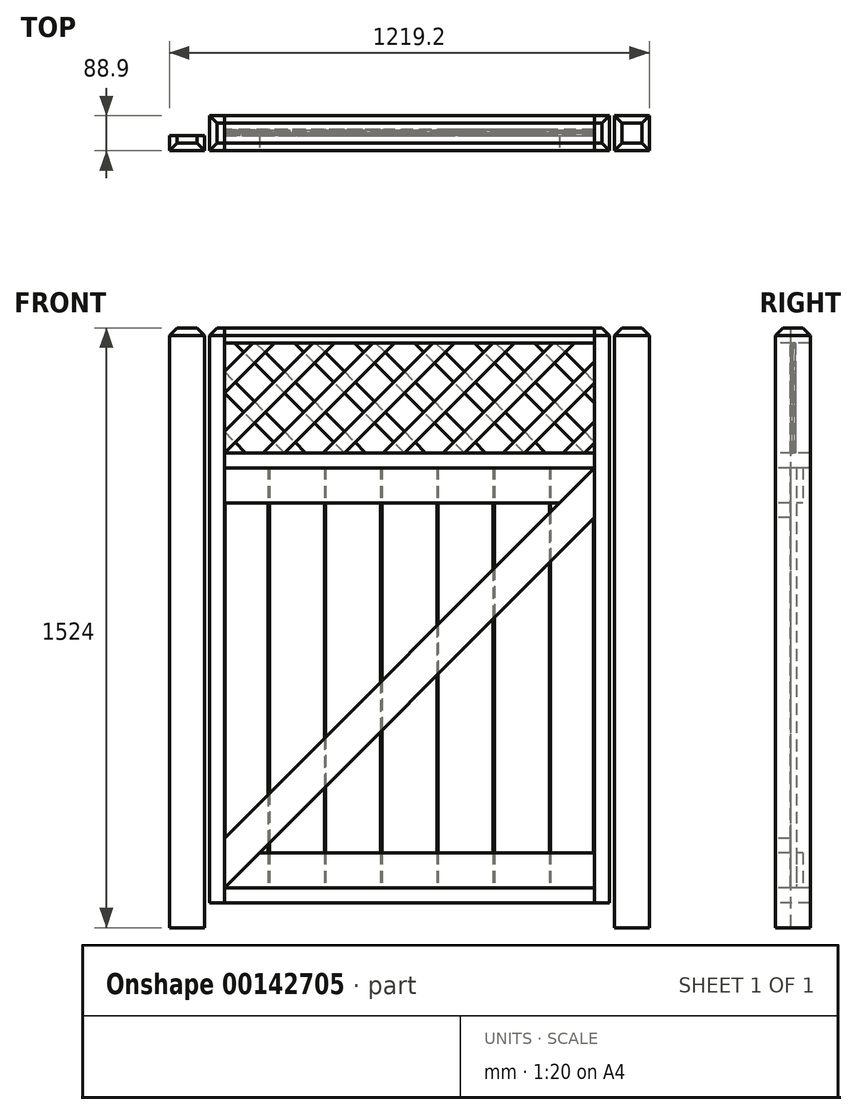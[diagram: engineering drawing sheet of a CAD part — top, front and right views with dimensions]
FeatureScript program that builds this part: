
annotation { "Feature Type Name" : "Feature", "Feature Type Description" : "" }
export const myFeature = defineFeature(function(context is Context, id is Id, definition is map)
    precondition{}
    {
        {
            var Q0;
            Q0=qCreatedBy(makeId("Top.planeOp"),FACE);
            var sketch = newSketch(context, id + "F0", { "sketchPlane" : qUnion([Q0])});
            skLineSegment(sketch, "E0", {"start": v(0, 0) * mm, "end": v(1250.95, 0) * mm, "construction": true});
            skLineSegment(sketch, "E1.bottom", {"start": v(1041.4, 0) * mm, "end": v(1130.3, 0) * mm});
            skLineSegment(sketch, "E1.top", {"start": v(1041.4, 88.9) * mm, "end": v(1130.3, 88.9) * mm});
            skLineSegment(sketch, "E1.left", {"start": v(1041.4, 0) * mm, "end": v(1041.4, 88.9) * mm});
            skLineSegment(sketch, "E1.right", {"start": v(1130.3, 0) * mm, "end": v(1130.3, 88.9) * mm});
            skLineSegment(sketch, "E2.bottom", {"start": v(0, 0) * mm, "end": v(-88.9, 0) * mm});
            skLineSegment(sketch, "E2.top", {"start": v(0, 38.1) * mm, "end": v(-88.9, 38.1) * mm});
            skLineSegment(sketch, "E2.left", {"start": v(0, 0) * mm, "end": v(0, 38.1) * mm});
            skLineSegment(sketch, "E2.right", {"start": v(-88.9, 0) * mm, "end": v(-88.9, 38.1) * mm});
            skSolve(sketch);
        }
        {
            var Q0;
            Q0 = qSketchRegion(id + "F0", true);
            extrude(context, id + "F1", {"entities" : qUnion([Q0]), "depth" : 1524 * mm});
        }
        {
            var Q0;
            Q0=makeQuery(id+"F1.opExtrude","SWEPT_FACE",FACE,{"disambiguationData":[OSD([sQuery(id+"F0.wireOp",EDGE,"E1.bottom")])]});
            var sketch = newSketch(context, id + "F2", { "sketchPlane" : qUnion([Q0])});
            skLineSegment(sketch, "E3.bottom", {"start": v(1028.7, 1524) * mm, "end": v(990.6, 1524) * mm});
            skLineSegment(sketch, "E3.top", {"start": v(1028.7, 63.5) * mm, "end": v(990.6, 63.5) * mm});
            skLineSegment(sketch, "E3.left", {"start": v(1028.7, 1524) * mm, "end": v(1028.7, 63.5) * mm});
            skLineSegment(sketch, "E3.right", {"start": v(990.6, 1524) * mm, "end": v(990.6, 63.5) * mm});
            skLineSegment(sketch, "E4.bottom", {"start": v(990.6, 1524) * mm, "end": v(50.8, 1524) * mm, "construction": true});
            skLineSegment(sketch, "E4.top", {"start": v(990.6, 1485.9) * mm, "end": v(50.8, 1485.9) * mm, "construction": true});
            skLineSegment(sketch, "E4.left", {"start": v(990.6, 1524) * mm, "end": v(990.6, 1485.9) * mm});
            skLineSegment(sketch, "E4.right", {"start": v(50.8, 1524) * mm, "end": v(50.8, 1485.9) * mm});
            skLineSegment(sketch, "E5.bottom", {"start": v(990.6, 63.5) * mm, "end": v(50.8, 63.5) * mm, "construction": true});
            skLineSegment(sketch, "E5.top", {"start": v(990.6, 101.6) * mm, "end": v(50.8, 101.6) * mm, "construction": true});
            skLineSegment(sketch, "E5.left", {"start": v(990.6, 63.5) * mm, "end": v(990.6, 101.6) * mm});
            skLineSegment(sketch, "E5.right", {"start": v(50.8, 63.5) * mm, "end": v(50.8, 101.6) * mm});
            skLineSegment(sketch, "E6.bottom", {"start": v(990.6, 1206.5) * mm, "end": v(50.8, 1206.5) * mm, "construction": true});
            skLineSegment(sketch, "E6.top", {"start": v(990.6, 1168.4) * mm, "end": v(50.8, 1168.4) * mm, "construction": true});
            skLineSegment(sketch, "E6.left", {"start": v(990.6, 1206.5) * mm, "end": v(990.6, 1168.4) * mm});
            skLineSegment(sketch, "E6.right", {"start": v(50.8, 1206.5) * mm, "end": v(50.8, 1168.4) * mm});
            skLineSegment(sketch, "E7.bottom", {"start": v(50.8, 1524) * mm, "end": v(12.7, 1524) * mm});
            skLineSegment(sketch, "E7.top", {"start": v(50.8, 63.5) * mm, "end": v(12.7, 63.5) * mm});
            skLineSegment(sketch, "E7.left", {"start": v(50.8, 1524) * mm, "end": v(50.8, 63.5) * mm});
            skLineSegment(sketch, "E7.right", {"start": v(12.7, 1524) * mm, "end": v(12.7, 63.5) * mm});
            skLineSegment(sketch, "E8", {"start": v(990.6, 1168.4) * mm, "end": v(50.8, 101.6) * mm, "construction": true});
            skLineSegment(sketch, "E9", {"start": v(990.6, 1110.76) * mm, "end": v(101.58, 101.6) * mm, "construction": true});
            skSolve(sketch);
        }
        {
            var Q0;
            Q0 = qSketchRegion(id + "F2", true);
            var Q1;
            {var subQ0=sQuery(id+"F2.wireOp",EDGE,"E8");Q1=makeQuery(id+"F2.imprint","IMPRINT",FACE,{"disambiguationData":[TD([[makeQuery(id+"F2.imprint","IMPRINT",EDGE,{"derivedFrom":subQ0}),1.0]])]});}
            var Q2;
            {var subQ0=sQuery(id+"F2.wireOp",EDGE,"E6.bottom");Q2=makeQuery(id+"F2.imprint","IMPRINT",FACE,{"disambiguationData":[TD([[makeQuery(id+"F2.imprint","IMPRINT",EDGE,{"derivedFrom":subQ0}),1.0]])]});}
            extrude(context, id + "F3", {"entities" : qUnion([Q0, Q1, Q2]), "oppositeDirection" : true, "depth" : 88.9 * mm});
        }
        {
            var Q0;
            Q0=makeQuery(id+"F1.opExtrude","SWEPT_FACE",FACE,{"disambiguationData":[OSD([sQuery(id+"F0.wireOp",EDGE,"E1.bottom")])]});
            var sketch = newSketch(context, id + "F4", { "sketchPlane" : qUnion([Q0])});
            skLineSegment(sketch, "E10.bottom", {"start": v(990.6, 1524) * mm, "end": v(50.8, 1524) * mm});
            skLineSegment(sketch, "E10.top", {"start": v(990.6, 1485.9) * mm, "end": v(50.8, 1485.9) * mm});
            skLineSegment(sketch, "E10.left", {"start": v(990.6, 1524) * mm, "end": v(990.6, 1485.9) * mm});
            skLineSegment(sketch, "E10.right", {"start": v(50.8, 1524) * mm, "end": v(50.8, 1485.9) * mm});
            skLineSegment(sketch, "E11.bottom", {"start": v(50.8, 1206.5) * mm, "end": v(990.6, 1206.5) * mm});
            skLineSegment(sketch, "E11.top", {"start": v(50.8, 1168.4) * mm, "end": v(990.6, 1168.4) * mm});
            skLineSegment(sketch, "E11.left", {"start": v(50.8, 1206.5) * mm, "end": v(50.8, 1168.4) * mm});
            skLineSegment(sketch, "E11.right", {"start": v(990.6, 1206.5) * mm, "end": v(990.6, 1168.4) * mm});
            skLineSegment(sketch, "E12.bottom", {"start": v(50.8, 63.5) * mm, "end": v(990.6, 63.5) * mm});
            skLineSegment(sketch, "E12.top", {"start": v(50.8, 101.6) * mm, "end": v(990.6, 101.6) * mm});
            skLineSegment(sketch, "E12.left", {"start": v(50.8, 63.5) * mm, "end": v(50.8, 101.6) * mm});
            skLineSegment(sketch, "E12.right", {"start": v(990.6, 63.5) * mm, "end": v(990.6, 101.6) * mm});
            skSolve(sketch);
        }
        {
            var Q0;
            Q0 = qSketchRegion(id + "F4", true);
            extrude(context, id + "F5", {"entities" : qUnion([Q0]), "oppositeDirection" : true, "depth" : 88.9 * mm});
        }
        {
            var Q0;
            {var subQ0=sQuery(id+"F0.wireOp",EDGE,"E1.bottom");Q0=makeQuery(id+"F2.imprint","IMPRINT",FACE,{"disambiguationData":[TD([[makeQuery(id+"F2.imprint","IMPRINT",EDGE,{"derivedFrom":makeQuery(id+"F1.opExtrude","CAP_EDGE",EDGE,{"disambiguationData":[OSD([subQ0])],"isStart":true})}),1.0]])]});}
            var sketch = newSketch(context, id + "F6", { "sketchPlane" : qUnion([Q0])});
            skLineSegment(sketch, "E13", {"start": v(990.6, 1168.4) * mm, "end": v(990.6, 1042.6) * mm});
            skLineSegment(sketch, "E14", {"start": v(990.6, 1042.6) * mm, "end": v(50.8, 101.6) * mm});
            skLineSegment(sketch, "E15", {"start": v(50.8, 101.6) * mm, "end": v(50.8, 227.4) * mm});
            skLineSegment(sketch, "E16", {"start": v(50.8, 227.4) * mm, "end": v(990.6, 1168.4) * mm});
            skSolve(sketch);
        }
        {
            var Q0;
            Q0 = qSketchRegion(id + "F6", true);
            extrude(context, id + "F7", {"entities" : qUnion([Q0]), "oppositeDirection" : true, "depth" : 38.1 * mm});
        }
        {
            var Q0;
            Q0=makeQuery(id+"F1.opExtrude","SWEPT_FACE",FACE,{"disambiguationData":[OSD([sQuery(id+"F0.wireOp",EDGE,"E1.bottom")])]});
            var sketch = newSketch(context, id + "F8", { "sketchPlane" : qUnion([Q0])});
            skLineSegment(sketch, "E17.bottom", {"start": v(50.8, 1168.4) * mm, "end": v(990.6, 1168.4) * mm});
            skLineSegment(sketch, "E17.top", {"start": v(50.8, 1079.5) * mm, "end": v(901.81, 1079.5) * mm});
            skLineSegment(sketch, "E17.left", {"start": v(50.8, 1168.4) * mm, "end": v(50.8, 1079.5) * mm});
            skLineSegment(sketch, "E18.bottom", {"start": v(990.6, 101.6) * mm, "end": v(50.8, 101.6) * mm});
            skLineSegment(sketch, "E18.top", {"start": v(990.6, 190.5) * mm, "end": v(139.59, 190.5) * mm});
            skLineSegment(sketch, "E18.left", {"start": v(990.6, 101.6) * mm, "end": v(990.6, 190.5) * mm});
            skLineSegment(sketch, "E19", {"start": v(990.6, 1168.4) * mm, "end": v(901.81, 1079.5) * mm});
            skLineSegment(sketch, "E20", {"start": v(50.8, 101.6) * mm, "end": v(139.59, 190.5) * mm});
            skSolve(sketch);
        }
        {
            var Q0;
            Q0 = qSketchRegion(id + "F8", true);
            extrude(context, id + "F9", {"entities" : qUnion([Q0]), "oppositeDirection" : true, "depth" : 38.1 * mm});
        }
        {
            var Q0;
            Q0=makeQuery(id+"F7.opExtrude","CAP_FACE",FACE,{"disambiguationData":[OSD([sQuery(id+"F6.wireOp",EDGE,"E13"),sQuery(id+"F6.wireOp",EDGE,"E14"),sQuery(id+"F6.wireOp",EDGE,"E15"),sQuery(id+"F6.wireOp",EDGE,"E16")])],"isStart":false});
            var sketch = newSketch(context, id + "F10", { "sketchPlane" : qUnion([Q0])});
            skLineSegment(sketch, "E21.left", {"start": v(-990.6, 1168.4) * mm, "end": v(-990.6, 101.6) * mm, "construction": true});
            skLineSegment(sketch, "E21.right", {"start": v(-50.8, 1168.4) * mm, "end": v(-50.8, 101.6) * mm, "construction": true});
            skLineSegment(sketch, "E22", {"start": v(-520.7, 1168.4) * mm, "end": v(-520.7, 101.6) * mm, "construction": true});
            skLineSegment(sketch, "E23", {"start": v(-990.6, 635) * mm, "end": v(-50.8, 635) * mm, "construction": true});
            skLineSegment(sketch, "E24.bottom", {"start": v(-450.85, 1168.4) * mm, "end": v(-590.55, 1168.4) * mm});
            skLineSegment(sketch, "E24.top", {"start": v(-450.85, 101.6) * mm, "end": v(-590.55, 101.6) * mm});
            skLineSegment(sketch, "E24.left", {"start": v(-450.85, 1168.4) * mm, "end": v(-450.85, 101.6) * mm});
            skLineSegment(sketch, "E24.right", {"start": v(-590.55, 1168.4) * mm, "end": v(-590.55, 101.6) * mm});
            skPoint(sketch, "E24.middle", {"position": v(-520.7, 635) * mm});
            skLineSegment(sketch, "E25.1.0.0", {"start": v(-307.98, 1168.4) * mm, "end": v(-307.98, 101.6) * mm});
            skLineSegment(sketch, "E25.1.0.1", {"start": v(-447.68, 1168.4) * mm, "end": v(-447.68, 101.6) * mm});
            skLineSegment(sketch, "E25.2.0.0", {"start": v(-165.1, 1168.4) * mm, "end": v(-165.1, 101.6) * mm});
            skLineSegment(sketch, "E25.2.0.1", {"start": v(-304.8, 1168.4) * mm, "end": v(-304.8, 101.6) * mm});
            skLineSegment(sketch, "E25.3.0.1", {"start": v(-161.93, 1168.4) * mm, "end": v(-161.93, 101.6) * mm});
            skLineSegment(sketch, "E25.direction1", {"start": v(-450.85, 101.6) * mm, "end": v(-307.98, 101.6) * mm, "construction": true});
            skLineSegment(sketch, "E26.MirrorCS", {"start": v(-876.3, 1168.4) * mm, "end": v(-876.3, 101.6) * mm});
            skLineSegment(sketch, "E27.MirrorCS", {"start": v(-879.48, 1168.4) * mm, "end": v(-879.48, 101.6) * mm});
            skLineSegment(sketch, "E28.MirrorCS", {"start": v(-736.6, 1168.4) * mm, "end": v(-736.6, 101.6) * mm});
            skLineSegment(sketch, "E29.MirrorCS", {"start": v(-593.73, 1168.4) * mm, "end": v(-593.73, 101.6) * mm});
            skLineSegment(sketch, "E30.MirrorCS", {"start": v(-733.43, 1168.4) * mm, "end": v(-733.43, 101.6) * mm});
            skLineSegment(sketch, "E31", {"start": v(-989.01, 1168.4) * mm, "end": v(-989.01, 101.6) * mm});
            skLineSegment(sketch, "E32", {"start": v(-52.39, 1168.4) * mm, "end": v(-52.39, 101.6) * mm});
            skLineSegment(sketch, "E33", {"start": v(-989.01, 1168.4) * mm, "end": v(-879.48, 1168.4) * mm});
            skLineSegment(sketch, "E34", {"start": v(-876.3, 1168.4) * mm, "end": v(-736.6, 1168.4) * mm});
            skLineSegment(sketch, "E35", {"start": v(-733.43, 1168.4) * mm, "end": v(-593.73, 1168.4) * mm});
            skLineSegment(sketch, "E36", {"start": v(-447.68, 1168.4) * mm, "end": v(-307.98, 1168.4) * mm});
            skLineSegment(sketch, "E37", {"start": v(-304.8, 1168.4) * mm, "end": v(-165.1, 1168.4) * mm});
            skLineSegment(sketch, "E38", {"start": v(-52.39, 1168.4) * mm, "end": v(-161.93, 1168.4) * mm});
            skLineSegment(sketch, "E39", {"start": v(-989.01, 101.6) * mm, "end": v(-879.48, 101.6) * mm});
            skLineSegment(sketch, "E40", {"start": v(-876.3, 101.6) * mm, "end": v(-736.6, 101.6) * mm});
            skLineSegment(sketch, "E41", {"start": v(-733.43, 101.6) * mm, "end": v(-593.73, 101.6) * mm});
            skLineSegment(sketch, "E42", {"start": v(-447.68, 101.6) * mm, "end": v(-307.98, 101.6) * mm});
            skLineSegment(sketch, "E43", {"start": v(-165.1, 101.6) * mm, "end": v(-304.8, 101.6) * mm});
            skLineSegment(sketch, "E44", {"start": v(-161.93, 101.6) * mm, "end": v(-52.39, 101.6) * mm});
            skSolve(sketch);
        }
        {
            var Q0;
            Q0 = qSketchRegion(id + "F10", true);
            extrude(context, id + "F11", {"entities" : qUnion([Q0]), "depth" : 15.88 * mm});
        }
        {
            var Q0;
            Q0=makeQuery(id+"F11.opExtrude","CAP_FACE",FACE,{"disambiguationData":[OSD([sQuery(id+"F10.wireOp",EDGE,"E27.MirrorCS"),sQuery(id+"F10.wireOp",EDGE,"E31"),sQuery(id+"F10.wireOp",EDGE,"E33"),sQuery(id+"F10.wireOp",EDGE,"E39")])],"isStart":false});
            var sketch = newSketch(context, id + "F12", { "sketchPlane" : qUnion([Q0])});
            skLineSegment(sketch, "E45.bottom", {"start": v(-990.6, 1168.4) * mm, "end": v(-50.8, 1168.4) * mm});
            skLineSegment(sketch, "E45.top", {"start": v(-990.6, 1079.5) * mm, "end": v(-50.8, 1079.5) * mm});
            skLineSegment(sketch, "E45.left", {"start": v(-990.6, 1168.4) * mm, "end": v(-990.6, 1079.5) * mm});
            skLineSegment(sketch, "E45.right", {"start": v(-50.8, 1168.4) * mm, "end": v(-50.8, 1079.5) * mm});
            skLineSegment(sketch, "E46.bottom", {"start": v(-990.6, 190.5) * mm, "end": v(-50.8, 190.5) * mm});
            skLineSegment(sketch, "E46.top", {"start": v(-990.6, 101.6) * mm, "end": v(-50.8, 101.6) * mm});
            skLineSegment(sketch, "E46.left", {"start": v(-990.6, 190.5) * mm, "end": v(-990.6, 101.6) * mm});
            skLineSegment(sketch, "E46.right", {"start": v(-50.8, 190.5) * mm, "end": v(-50.8, 101.6) * mm});
            skSolve(sketch);
        }
        {
            var Q0;
            Q0 = qSketchRegion(id + "F12", true);
            extrude(context, id + "F13", {"entities" : qUnion([Q0]), "depth" : 15.88 * mm});
        }
        {
            var Q0;
            Q0=makeQuery(id+"F3.opExtrude","CAP_FACE",FACE,{"disambiguationData":[OSD([sQuery(id+"F2.wireOp",EDGE,"E3.bottom"),sQuery(id+"F2.wireOp",EDGE,"E3.top"),sQuery(id+"F2.wireOp",EDGE,"E3.left"),sQuery(id+"F2.wireOp",EDGE,"E3.right"),sQuery(id+"F2.wireOp",EDGE,"E4.left"),sQuery(id+"F2.wireOp",EDGE,"E5.left"),sQuery(id+"F2.wireOp",EDGE,"E6.left")])],"isStart":true});
            cPlane(context, id + "F14", {"entities" : qUnion([Q0]), "cplaneType" : CPlaneType.OFFSET, "offset" : 44.45 * mm, "oppositeDirection" : true, "width" : 152.4 * mm, "height" : 152.4 * mm});
        }
        {
            var Q0;
            Q0=qCreatedBy(id+"F14.planeOp",FACE);
            var sketch = newSketch(context, id + "F15", { "sketchPlane" : qUnion([Q0])});
            skLineSegment(sketch, "E47.bottom", {"start": v(123.92, 1485.9) * mm, "end": v(177.8, 1485.9) * mm});
            skLineSegment(sketch, "E47.left", {"start": v(50.8, 1412.78) * mm, "end": v(50.8, 1358.9) * mm});
            skLineSegment(sketch, "E47.right", {"start": v(990.6, 1438.18) * mm, "end": v(990.6, 1384.3) * mm});
            skLineSegment(sketch, "E48", {"start": v(50.8, 1206.5) * mm, "end": v(330.2, 1485.9) * mm});
            skLineSegment(sketch, "E49", {"start": v(276.32, 1485.9) * mm, "end": v(50.8, 1260.38) * mm});
            skLineSegment(sketch, "E50.1.0.0", {"start": v(203.2, 1206.5) * mm, "end": v(482.6, 1485.9) * mm});
            skLineSegment(sketch, "E50.1.0.1", {"start": v(428.72, 1485.9) * mm, "end": v(149.32, 1206.5) * mm});
            skLineSegment(sketch, "E50.2.0.0", {"start": v(355.6, 1206.5) * mm, "end": v(635, 1485.9) * mm});
            skLineSegment(sketch, "E50.2.0.1", {"start": v(581.12, 1485.9) * mm, "end": v(301.72, 1206.5) * mm});
            skLineSegment(sketch, "E50.3.0.0", {"start": v(508, 1206.5) * mm, "end": v(787.4, 1485.9) * mm});
            skLineSegment(sketch, "E50.3.0.1", {"start": v(733.52, 1485.9) * mm, "end": v(454.12, 1206.5) * mm});
            skLineSegment(sketch, "E50.4.0.0", {"start": v(660.4, 1206.5) * mm, "end": v(939.8, 1485.9) * mm});
            skLineSegment(sketch, "E50.4.0.1", {"start": v(885.92, 1485.9) * mm, "end": v(606.52, 1206.5) * mm});
            skLineSegment(sketch, "E50.5.0.0", {"start": v(812.8, 1206.5) * mm, "end": v(990.6, 1384.3) * mm});
            skLineSegment(sketch, "E50.5.0.1", {"start": v(990.6, 1438.18) * mm, "end": v(758.92, 1206.5) * mm});
            skLineSegment(sketch, "E50.6.0.0", {"start": v(965.2, 1206.5) * mm, "end": v(990.6, 1231.9) * mm});
            skLineSegment(sketch, "E50.6.0.1", {"start": v(990.6, 1285.78) * mm, "end": v(911.32, 1206.5) * mm});
            skLineSegment(sketch, "E51.1.0.0", {"start": v(50.8, 1358.9) * mm, "end": v(177.8, 1485.9) * mm});
            skLineSegment(sketch, "E51.1.0.1", {"start": v(123.92, 1485.9) * mm, "end": v(50.8, 1412.78) * mm});
            skLineSegment(sketch, "E52.trimOffspring", {"start": v(50.8, 1260.38) * mm, "end": v(50.8, 1206.5) * mm});
            skLineSegment(sketch, "E53.trimOffspring", {"start": v(276.32, 1485.9) * mm, "end": v(330.2, 1485.9) * mm});
            skLineSegment(sketch, "E54.trimOffspring", {"start": v(301.72, 1206.5) * mm, "end": v(355.6, 1206.5) * mm});
            skLineSegment(sketch, "E55.trimOffspring", {"start": v(581.12, 1485.9) * mm, "end": v(635, 1485.9) * mm});
            skLineSegment(sketch, "E56.trimOffspring", {"start": v(990.6, 1285.78) * mm, "end": v(990.6, 1231.9) * mm});
            skLineSegment(sketch, "E57.trimOffspring", {"start": v(911.32, 1206.5) * mm, "end": v(965.2, 1206.5) * mm});
            skLineSegment(sketch, "E58.trimOffspring", {"start": v(758.92, 1206.5) * mm, "end": v(812.8, 1206.5) * mm});
            skLineSegment(sketch, "E59.trimOffspring", {"start": v(885.92, 1485.9) * mm, "end": v(939.8, 1485.9) * mm});
            skLineSegment(sketch, "E60.trimOffspring", {"start": v(733.52, 1485.9) * mm, "end": v(787.4, 1485.9) * mm});
            skLineSegment(sketch, "E61.trimOffspring", {"start": v(454.12, 1206.5) * mm, "end": v(508, 1206.5) * mm});
            skLineSegment(sketch, "E62.trimOffspring", {"start": v(606.52, 1206.5) * mm, "end": v(660.4, 1206.5) * mm});
            skLineSegment(sketch, "E63", {"start": v(203.2, 1206.5) * mm, "end": v(149.32, 1206.5) * mm});
            skLineSegment(sketch, "E64", {"start": v(177.8, 1485.9) * mm, "end": v(123.92, 1485.9) * mm});
            skLineSegment(sketch, "E65", {"start": v(428.72, 1485.9) * mm, "end": v(482.6, 1485.9) * mm});
            skSolve(sketch);
        }
        {
            var Q0;
            Q0 = qSketchRegion(id + "F15", true);
            extrude(context, id + "F16", {"entities" : qUnion([Q0]), "depth" : 6.35 * mm});
        }
        {
            var Q0;
            Q0=qCreatedBy(id+"F14.planeOp",FACE);
            var sketch = newSketch(context, id + "F17", { "sketchPlane" : qUnion([Q0])});
            skLineSegment(sketch, "E66", {"start": v(50.8, 1260.38) * mm, "end": v(104.68, 1206.5) * mm});
            skLineSegment(sketch, "E67", {"start": v(104.68, 1206.5) * mm, "end": v(50.8, 1206.5) * mm});
            skLineSegment(sketch, "E68.1.0.0", {"start": v(50.8, 1412.78) * mm, "end": v(257.08, 1206.5) * mm});
            skLineSegment(sketch, "E68.1.0.2", {"start": v(203.2, 1206.5) * mm, "end": v(50.8, 1358.9) * mm});
            skLineSegment(sketch, "E68.1.0.3", {"start": v(257.08, 1206.5) * mm, "end": v(203.2, 1206.5) * mm});
            skLineSegment(sketch, "E68.2.0.0", {"start": v(130.08, 1485.9) * mm, "end": v(409.48, 1206.5) * mm});
            skLineSegment(sketch, "E68.2.0.1", {"start": v(76.2, 1485.9) * mm, "end": v(130.08, 1485.9) * mm});
            skLineSegment(sketch, "E68.2.0.2", {"start": v(355.6, 1206.5) * mm, "end": v(76.2, 1485.9) * mm});
            skLineSegment(sketch, "E68.2.0.3", {"start": v(409.48, 1206.5) * mm, "end": v(355.6, 1206.5) * mm});
            skLineSegment(sketch, "E68.3.0.0", {"start": v(282.48, 1485.9) * mm, "end": v(561.88, 1206.5) * mm});
            skLineSegment(sketch, "E68.3.0.1", {"start": v(228.6, 1485.9) * mm, "end": v(282.48, 1485.9) * mm});
            skLineSegment(sketch, "E68.3.0.2", {"start": v(508, 1206.5) * mm, "end": v(228.6, 1485.9) * mm});
            skLineSegment(sketch, "E68.3.0.3", {"start": v(561.88, 1206.5) * mm, "end": v(508, 1206.5) * mm});
            skLineSegment(sketch, "E68.4.0.0", {"start": v(434.88, 1485.9) * mm, "end": v(714.28, 1206.5) * mm});
            skLineSegment(sketch, "E68.4.0.1", {"start": v(381, 1485.9) * mm, "end": v(434.88, 1485.9) * mm});
            skLineSegment(sketch, "E68.4.0.2", {"start": v(660.4, 1206.5) * mm, "end": v(381, 1485.9) * mm});
            skLineSegment(sketch, "E68.4.0.3", {"start": v(714.28, 1206.5) * mm, "end": v(660.4, 1206.5) * mm});
            skLineSegment(sketch, "E68.5.0.0", {"start": v(587.28, 1485.9) * mm, "end": v(866.68, 1206.5) * mm});
            skLineSegment(sketch, "E68.5.0.1", {"start": v(533.4, 1485.9) * mm, "end": v(587.28, 1485.9) * mm});
            skLineSegment(sketch, "E68.5.0.2", {"start": v(812.8, 1206.5) * mm, "end": v(533.4, 1485.9) * mm});
            skLineSegment(sketch, "E68.5.0.3", {"start": v(866.68, 1206.5) * mm, "end": v(812.8, 1206.5) * mm});
            skLineSegment(sketch, "E68.6.0.0", {"start": v(739.68, 1485.9) * mm, "end": v(990.6, 1234.98) * mm});
            skLineSegment(sketch, "E68.6.0.1", {"start": v(685.8, 1485.9) * mm, "end": v(739.68, 1485.9) * mm});
            skLineSegment(sketch, "E68.6.0.2", {"start": v(965.2, 1206.5) * mm, "end": v(685.8, 1485.9) * mm});
            skLineSegment(sketch, "E68.6.0.3", {"start": v(990.6, 1206.5) * mm, "end": v(965.2, 1206.5) * mm});
            skLineSegment(sketch, "E68.7.0.0", {"start": v(892.08, 1485.9) * mm, "end": v(990.6, 1387.38) * mm});
            skLineSegment(sketch, "E68.7.0.1", {"start": v(838.2, 1485.9) * mm, "end": v(892.08, 1485.9) * mm});
            skLineSegment(sketch, "E68.7.0.2", {"start": v(990.6, 1333.5) * mm, "end": v(838.2, 1485.9) * mm});
            skLineSegment(sketch, "E68.direction1", {"start": v(104.68, 1206.5) * mm, "end": v(257.08, 1206.5) * mm, "construction": true});
            skLineSegment(sketch, "E69", {"start": v(50.8, 1412.78) * mm, "end": v(50.8, 1358.9) * mm});
            skLineSegment(sketch, "E70.trimOffspring", {"start": v(50.8, 1260.38) * mm, "end": v(50.8, 1206.5) * mm});
            skLineSegment(sketch, "E71", {"start": v(990.6, 1387.38) * mm, "end": v(990.6, 1333.5) * mm});
            skLineSegment(sketch, "E72.trimOffspring", {"start": v(990.6, 1234.98) * mm, "end": v(990.6, 1206.5) * mm});
            skSolve(sketch);
        }
        {
            var Q0;
            Q0 = qSketchRegion(id + "F17", true);
            extrude(context, id + "F18", {"entities" : qUnion([Q0]), "oppositeDirection" : true, "depth" : 6.35 * mm});
        }
        {
            var Q0;
            Q0=makeQuery(id+"F5.opExtrude","CAP_EDGE",EDGE,{"disambiguationData":[OSD([sQuery(id+"F4.wireOp",EDGE,"E10.bottom")])],"isStart":true});
            var Q1;
            Q1=makeQuery(id+"F3.opExtrude","CAP_EDGE",EDGE,{"disambiguationData":[OSD([sQuery(id+"F2.wireOp",EDGE,"E3.bottom")])],"isStart":true});
            var Q2;
            Q2=makeQuery(id+"F3.opExtrude","SWEPT_EDGE",EDGE,{"disambiguationData":[OSD([sQuery(id+"F2.wireOp",EDGE,"E3.bottom"),sQuery(id+"F2.wireOp",EDGE,"E3.left")])]});
            var Q3;
            Q3=makeQuery(id+"F5.opExtrude","CAP_EDGE",EDGE,{"disambiguationData":[OSD([sQuery(id+"F4.wireOp",EDGE,"E10.bottom")])],"isStart":false});
            var Q4;
            Q4=makeQuery(id+"F3.opExtrude","CAP_EDGE",EDGE,{"disambiguationData":[OSD([sQuery(id+"F2.wireOp",EDGE,"E3.bottom")])],"isStart":false});
            var Q5;
            Q5=makeQuery(id+"F3.opExtrude","CAP_EDGE",EDGE,{"disambiguationData":[OSD([sQuery(id+"F2.wireOp",EDGE,"E7.bottom")])],"isStart":true});
            var Q6;
            Q6=makeQuery(id+"F3.opExtrude","SWEPT_EDGE",EDGE,{"disambiguationData":[OSD([sQuery(id+"F2.wireOp",EDGE,"E7.bottom"),sQuery(id+"F2.wireOp",EDGE,"E7.right")])]});
            var Q7;
            Q7=makeQuery(id+"F3.opExtrude","CAP_EDGE",EDGE,{"disambiguationData":[OSD([sQuery(id+"F2.wireOp",EDGE,"E7.bottom")])],"isStart":false});
            var Q8;
            Q8=makeQuery(id+"F1.opExtrude","CAP_FACE",FACE,{"disambiguationData":[OSD([sQuery(id+"F0.wireOp",EDGE,"E1.bottom"),sQuery(id+"F0.wireOp",EDGE,"E1.top"),sQuery(id+"F0.wireOp",EDGE,"E1.left"),sQuery(id+"F0.wireOp",EDGE,"E1.right")])],"isStart":false});
            var Q9;
            Q9=makeQuery(id+"F1.opExtrude","CAP_EDGE",EDGE,{"disambiguationData":[OSD([sQuery(id+"F0.wireOp",EDGE,"E2.bottom")])],"isStart":false});
            var Q10;
            Q10=makeQuery(id+"F1.opExtrude","CAP_EDGE",EDGE,{"disambiguationData":[OSD([sQuery(id+"F0.wireOp",EDGE,"E2.left")])],"isStart":false});
            var Q11;
            Q11=makeQuery(id+"F1.opExtrude","CAP_EDGE",EDGE,{"disambiguationData":[OSD([sQuery(id+"F0.wireOp",EDGE,"E2.right")])],"isStart":false});
            chamfer(context, id + "F19", {"entities" : qUnion([Q0, Q1, Q2, Q3, Q4, Q5, Q6, Q7, Q8, Q9, Q10, Q11]), "width" : 19.05 * mm, "tangentPropagation" : true});
        }
    });
